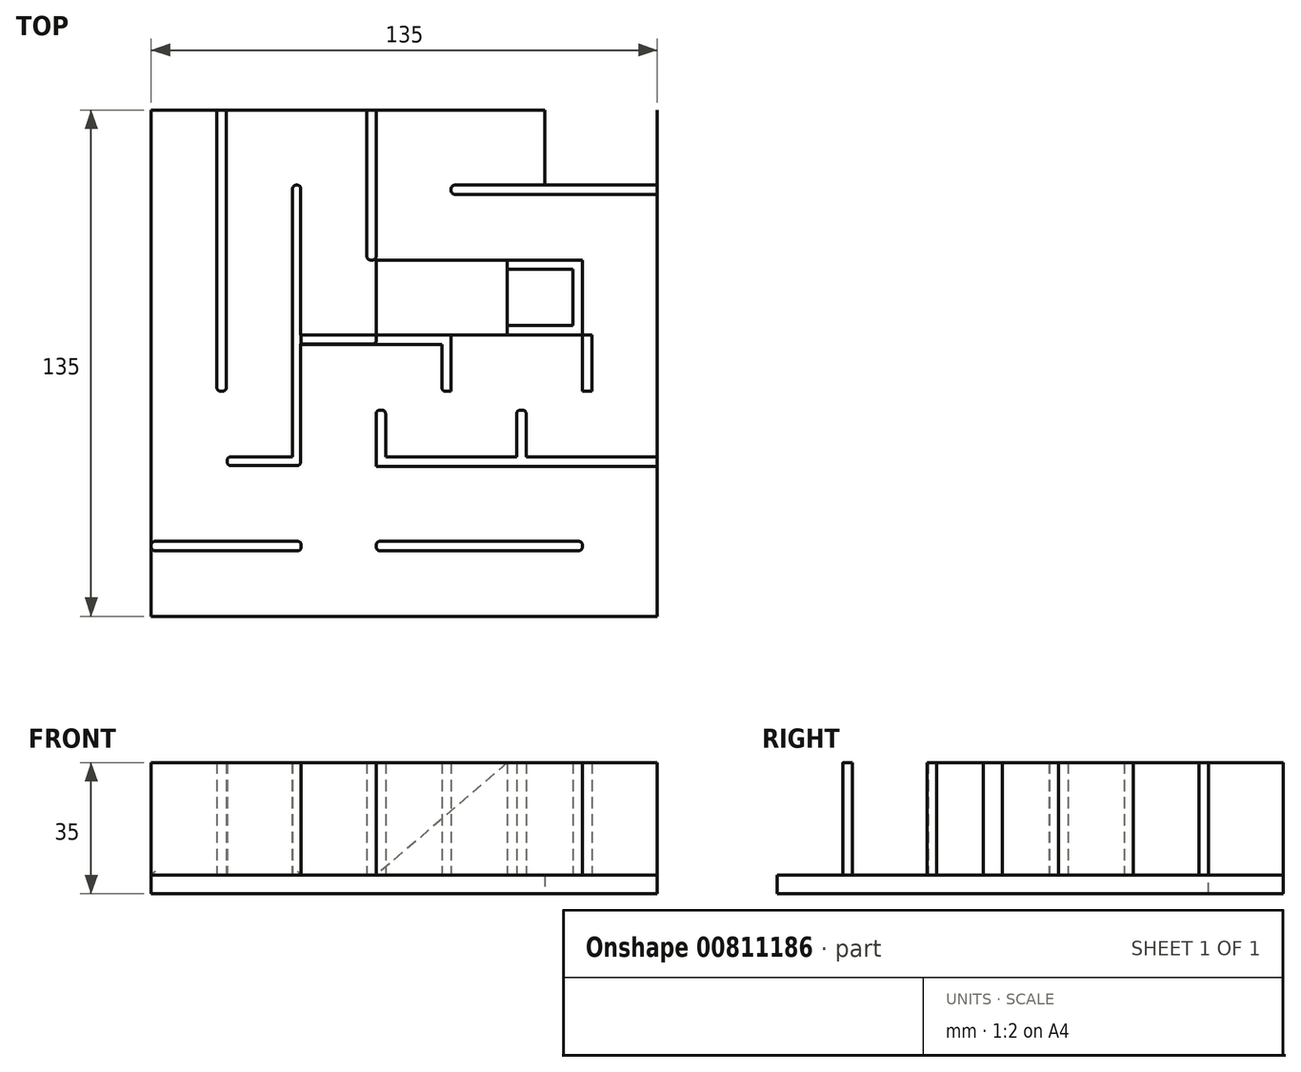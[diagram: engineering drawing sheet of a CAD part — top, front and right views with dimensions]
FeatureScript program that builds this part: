
annotation { "Feature Type Name" : "Feature", "Feature Type Description" : "" }
export const myFeature = defineFeature(function(context is Context, id is Id, definition is map)
    precondition{}
    {
        {
            var Q0;
            Q0=qCreatedBy(makeId("Top.planeOp"),FACE);
            var sketch = newSketch(context, id + "F0", { "sketchPlane" : qUnion([Q0])});
            skLineSegment(sketch, "E0.bottom", {"start": v(-67.5, 67.5) * mm, "end": v(67.5, 67.5) * mm});
            skLineSegment(sketch, "E0.top", {"start": v(-67.5, -67.5) * mm, "end": v(67.5, -67.5) * mm});
            skLineSegment(sketch, "E0.left", {"start": v(-67.5, 67.5) * mm, "end": v(-67.5, -67.5) * mm});
            skLineSegment(sketch, "E0.right", {"start": v(67.5, 67.5) * mm, "end": v(67.5, -67.5) * mm});
            skPoint(sketch, "E0.middle", {"position": v(0, 0) * mm});
            skSolve(sketch);
        }
        {
            var Q0;
            {var subQ2=sQuery(id+"F0.wireOp",EDGE,"E0.top");Q0=makeQuery(id+"F0.imprint","IMPRINT",FACE,{"disambiguationData":[TD([[makeQuery(id+"F0.imprint","IMPRINT",EDGE,{"derivedFrom":subQ2}),1.0]])]});}
            extrude(context, id + "F1", {"entities" : qUnion([Q0]), "depth" : 5 * mm, "offsetDistance" : 25 * mm});
        }
        {
            var Q0;
            Q0=makeQuery(id+"F1.opExtrude","CAP_FACE",FACE,{"disambiguationData":[OSD([sQuery(id+"F0.wireOp",EDGE,"E0.bottom"),sQuery(id+"F0.wireOp",EDGE,"E0.top"),sQuery(id+"F0.wireOp",EDGE,"E0.left"),sQuery(id+"F0.wireOp",EDGE,"E0.right"),sQuery(id+"F0.wireOp",EDGE,"C7zKFyMu-DAGJ-jgr1-EAXP-FvyqHJ8hfMsY"),sQuery(id+"F0.wireOp",EDGE,"vBC2NWEj-7rqq-zskN-MrQE-4xOVSqg6ddvG")])],"isStart":false});
            var sketch = newSketch(context, id + "F2", { "sketchPlane" : qUnion([Q0])});
            skSolve(sketch);
        }
        {
            var Q0;
            Q0=makeQuery(id+"F2.imprint","IMPRINT",FACE,{"disambiguationData":[TD([[makeQuery(id+"F2.imprint","IMPRINT",EDGE,{"derivedFrom":makeQuery(id+"F1.opExtrude","CAP_EDGE",EDGE,{"disambiguationData":[OSD([sQuery(id+"F0.wireOp",EDGE,"E0.bottom")])],"isStart":false})}),-1.0]])]});
            var sketch = newSketch(context, id + "F3", { "sketchPlane" : qUnion([Q0])});
            skLineSegment(sketch, "E1.bottom", {"start": v(-7.5, 27.5) * mm, "end": v(27.5, 27.5) * mm});
            skLineSegment(sketch, "E1.top", {"start": v(-7.5, 7.5) * mm, "end": v(27.5, 7.5) * mm});
            skLineSegment(sketch, "E1.left", {"start": v(-7.5, 27.5) * mm, "end": v(-7.5, 7.5) * mm});
            skLineSegment(sketch, "E1.right", {"start": v(27.5, 27.5) * mm, "end": v(27.5, 7.5) * mm});
            skLineSegment(sketch, "E2", {"start": v(-7.5, 7.5) * mm, "end": v(-27.5, 7.5) * mm});
            skLineSegment(sketch, "E3", {"start": v(-27.5, 7.5) * mm, "end": v(-27.5, 47.5) * mm});
            skLineSegment(sketch, "E4.bottom", {"start": v(-67.5, 67.5) * mm, "end": v(67.5, 67.5) * mm});
            skLineSegment(sketch, "E4.top", {"start": v(-67.5, -67.5) * mm, "end": v(67.5, -67.5) * mm});
            skLineSegment(sketch, "E4.left", {"start": v(-67.5, 67.5) * mm, "end": v(-67.5, -67.5) * mm});
            skLineSegment(sketch, "E4.right", {"start": v(67.5, 67.5) * mm, "end": v(67.5, -67.5) * mm});
            skPoint(sketch, "E4.middle", {"position": v(0, 0) * mm});
            skLineSegment(sketch, "E5", {"start": v(-47.5, 67.5) * mm, "end": v(-47.5, -7.5) * mm});
            skLineSegment(sketch, "E6.bottom", {"start": v(67.5, 67.5) * mm, "end": v(37.5, 67.5) * mm});
            skLineSegment(sketch, "E6.top", {"start": v(67.5, 47.5) * mm, "end": v(37.5, 47.5) * mm});
            skLineSegment(sketch, "E6.left", {"start": v(67.5, 67.5) * mm, "end": v(67.5, 47.5) * mm});
            skLineSegment(sketch, "E6.right", {"start": v(37.5, 67.5) * mm, "end": v(37.5, 47.5) * mm});
            skLineSegment(sketch, "E7", {"start": v(-27.5, 7.5) * mm, "end": v(-27.5, -27.5) * mm});
            skLineSegment(sketch, "E8", {"start": v(-27.5, -27.5) * mm, "end": v(-47.5, -27.5) * mm});
            skLineSegment(sketch, "E9", {"start": v(-67.5, -47.5) * mm, "end": v(-27.5, -47.5) * mm});
            skLineSegment(sketch, "E10", {"start": v(-7.5, -47.5) * mm, "end": v(47.5, -47.5) * mm});
            skLineSegment(sketch, "E11", {"start": v(67.5, -27.5) * mm, "end": v(-7.5, -27.5) * mm});
            skLineSegment(sketch, "E12", {"start": v(-7.5, -27.5) * mm, "end": v(-7.5, -12.5) * mm});
            skLineSegment(sketch, "E13", {"start": v(12.5, 7.63) * mm, "end": v(12.5, -7.5) * mm});
            skLineSegment(sketch, "E14", {"start": v(32.5, -27.5) * mm, "end": v(32.5, -12.5) * mm});
            skLineSegment(sketch, "E15", {"start": v(37.5, 47.5) * mm, "end": v(12.5, 47.5) * mm});
            skLineSegment(sketch, "E16", {"start": v(-7.5, 27.5) * mm, "end": v(-7.5, 67.5) * mm});
            skLineSegment(sketch, "E17.0", {"start": v(-5, -25) * mm, "end": v(-5, -12.5) * mm});
            skLineSegment(sketch, "E17.1", {"start": v(67.5, -25) * mm, "end": v(-5, -25) * mm});
            skLineSegment(sketch, "E18.0", {"start": v(-30, -25) * mm, "end": v(-47.5, -25) * mm});
            skLineSegment(sketch, "E18.1", {"start": v(-30, 7.5) * mm, "end": v(-30, -25) * mm});
            skLineSegment(sketch, "E18.2", {"start": v(-30, 7.5) * mm, "end": v(-30, 47.5) * mm});
            skLineSegment(sketch, "E19.0", {"start": v(-50, 67.5) * mm, "end": v(-50, -7.5) * mm});
            skLineSegment(sketch, "E20.0", {"start": v(-10, 27.5) * mm, "end": v(-10, 67.5) * mm});
            skLineSegment(sketch, "E21.0", {"start": v(-7.5, -50) * mm, "end": v(47.5, -50) * mm});
            skLineSegment(sketch, "E22.0", {"start": v(-67.5, -50) * mm, "end": v(-27.5, -50) * mm});
            skLineSegment(sketch, "E23.0", {"start": v(25.06, 45) * mm, "end": v(12.5, 45) * mm});
            skLineSegment(sketch, "E23.1", {"start": v(67.5, 45) * mm, "end": v(25.06, 45) * mm});
            skLineSegment(sketch, "E24.0", {"start": v(10, 7.63) * mm, "end": v(10, -7.5) * mm});
            skLineSegment(sketch, "E25.0", {"start": v(30, -27.5) * mm, "end": v(30, -12.5) * mm});
            skLineSegment(sketch, "E26.0", {"start": v(-7.5, 5) * mm, "end": v(-27.5, 5) * mm});
            skLineSegment(sketch, "E27", {"start": v(-47.5, -7.5) * mm, "end": v(-50, -7.5) * mm});
            skLineSegment(sketch, "E28", {"start": v(-5, -12.5) * mm, "end": v(-7.5, -12.5) * mm});
            skLineSegment(sketch, "E29", {"start": v(12.5, -7.5) * mm, "end": v(10, -7.5) * mm});
            skLineSegment(sketch, "E30", {"start": v(30, -12.5) * mm, "end": v(32.5, -12.5) * mm});
            skLineSegment(sketch, "E31", {"start": v(-47.5, -27.5) * mm, "end": v(-47.5, -25) * mm});
            skLineSegment(sketch, "E32", {"start": v(-10, 27.5) * mm, "end": v(-7.5, 27.5) * mm});
            skLineSegment(sketch, "E33", {"start": v(-27.5, 47.5) * mm, "end": v(-30, 47.5) * mm});
            skLineSegment(sketch, "E34", {"start": v(12.5, 45) * mm, "end": v(12.5, 47.5) * mm});
            skLineSegment(sketch, "E35", {"start": v(47.5, -50) * mm, "end": v(47.5, -47.5) * mm});
            skLineSegment(sketch, "E36", {"start": v(-7.5, -47.5) * mm, "end": v(-7.5, -50) * mm});
            skLineSegment(sketch, "E37", {"start": v(-27.5, -47.5) * mm, "end": v(-27.5, -50) * mm});
            skLineSegment(sketch, "E38", {"start": v(-27.5, -50) * mm, "end": v(-27.5, -47.5) * mm});
            skLineSegment(sketch, "E39", {"start": v(27.5, 7.5) * mm, "end": v(47.5, 7.5) * mm});
            skLineSegment(sketch, "E40", {"start": v(47.5, 7.5) * mm, "end": v(47.5, 27.5) * mm});
            skLineSegment(sketch, "E41", {"start": v(47.5, 27.5) * mm, "end": v(27.5, 27.5) * mm});
            skPoint(sketch, "E42.end.orphan", {"position": v(67.5, 27.5) * mm});
            skPoint(sketch, "E43.end.orphan", {"position": v(52.5, 27.5) * mm});
            skPoint(sketch, "E44.end.orphan", {"position": v(67.5, 25) * mm});
            skPoint(sketch, "E45.end.orphan", {"position": v(52.5, -7.5) * mm});
            skPoint(sketch, "E46.end.orphan", {"position": v(67.5, -7.5) * mm});
            skLineSegment(sketch, "E47.bottom", {"start": v(50, 7.5) * mm, "end": v(47.5, 7.5) * mm});
            skLineSegment(sketch, "E47.top", {"start": v(50, -7.5) * mm, "end": v(47.5, -7.5) * mm});
            skLineSegment(sketch, "E47.left", {"start": v(47.5, 7.5) * mm, "end": v(47.5, -7.5) * mm});
            skLineSegment(sketch, "E47.right", {"start": v(50, 7.5) * mm, "end": v(50, -7.5) * mm});
            skLineSegment(sketch, "E48", {"start": v(-7.5, 5) * mm, "end": v(10, 5) * mm});
            skLineSegment(sketch, "E49.bottom", {"start": v(27.5, 25) * mm, "end": v(45, 25) * mm});
            skLineSegment(sketch, "E49.top", {"start": v(27.5, 10) * mm, "end": v(45, 10) * mm});
            skLineSegment(sketch, "E49.left", {"start": v(27.5, 25) * mm, "end": v(27.5, 10) * mm});
            skLineSegment(sketch, "E49.right", {"start": v(45, 25) * mm, "end": v(45, 10) * mm});
            skSolve(sketch);
        }
        {
            var Q0;
            Q0=makeQuery(id+"F3.imprint","IMPRINT",FACE,{"disambiguationData":[TD([[makeQuery(id+"F3.imprint","IMPRINT",EDGE,{"derivedFrom":sQuery(id+"F3.wireOp",EDGE,"E1.bottom")}),-1.0]])]});
            extrude(context, id + "F4", {"entities" : qUnion([Q0]), "operationType" : NewBodyOperationType.ADD, "depth" : 30 * mm, "offsetDistance" : 25 * mm});
        }
        {
            var Q0;
            Q0=makeQuery(id+"F4.opExtrude","SWEPT_FACE",FACE,{"disambiguationData":[OSD([sQuery(id+"F3.wireOp",EDGE,"E1.top")])]});
            var sketch = newSketch(context, id + "F5", { "sketchPlane" : qUnion([Q0])});
            skLineSegment(sketch, "E50", {"start": v(27.5, 35) * mm, "end": v(-7.5, 5) * mm});
            skSolve(sketch);
        }
        {
            var Q0;
            Q0=makeQuery(id+"F5.imprint","IMPRINT",FACE,{"disambiguationData":[TD([[makeQuery(id+"F5.imprint","IMPRINT",EDGE,{"derivedFrom":sQuery(id+"F5.wireOp",EDGE,"E50")}),-1.0]])]});
            extrude(context, id + "F6", {"entities" : qUnion([Q0]), "operationType" : NewBodyOperationType.REMOVE, "oppositeDirection" : true, "depth" : 20 * mm, "offsetDistance" : 25 * mm});
        }
        {
            var Q0;
            Q0=makeQuery(id+"F3.imprint","IMPRINT",FACE,{"disambiguationData":[TD([[makeQuery(id+"F3.imprint","IMPRINT",EDGE,{"derivedFrom":sQuery(id+"F3.wireOp",EDGE,"E1.bottom")}),1.0]])]});
            var sketch = newSketch(context, id + "F7", { "sketchPlane" : qUnion([Q0])});
            skLineSegment(sketch, "E51", {"start": v(-7.48, 7.56) * mm, "end": v(-7.48, 5.1) * mm});
            skLineSegment(sketch, "E52", {"start": v(-7.48, 5.1) * mm, "end": v(-27.63, 5.1) * mm});
            skLineSegment(sketch, "E53", {"start": v(-27.63, 5.1) * mm, "end": v(-27.63, 7.49) * mm});
            skLineSegment(sketch, "E54", {"start": v(-27.63, 7.49) * mm, "end": v(-7.48, 7.56) * mm});
            skLineSegment(sketch, "E55", {"start": v(-27.63, 5.1) * mm, "end": v(-27.63, -27.3) * mm});
            skLineSegment(sketch, "E56", {"start": v(-27.63, -27.3) * mm, "end": v(-47.27, -27.3) * mm});
            skLineSegment(sketch, "E57", {"start": v(-47.27, -27.3) * mm, "end": v(-47.27, -24.93) * mm});
            skLineSegment(sketch, "E58", {"start": v(-47.27, -24.93) * mm, "end": v(-29.8, -24.93) * mm});
            skLineSegment(sketch, "E59", {"start": v(-29.8, -24.93) * mm, "end": v(-29.8, 47.57) * mm});
            skLineSegment(sketch, "E60", {"start": v(-29.8, 47.57) * mm, "end": v(-27.63, 47.57) * mm});
            skLineSegment(sketch, "E61", {"start": v(-27.63, 47.57) * mm, "end": v(-27.63, 7.49) * mm});
            skSolve(sketch);
        }
        {
            var Q0;
            Q0=makeQuery(id+"F2.imprint","IMPRINT",FACE,{"disambiguationData":[TD([[makeQuery(id+"F2.imprint","IMPRINT",EDGE,{"derivedFrom":makeQuery(id+"F1.opExtrude","CAP_EDGE",EDGE,{"disambiguationData":[OSD([sQuery(id+"F0.wireOp",EDGE,"E0.bottom")])],"isStart":false})}),-1.0]])]});
            var sketch = newSketch(context, id + "F8", { "sketchPlane" : qUnion([Q0])});
            skLineSegment(sketch, "E62", {"start": v(37.54, 47.53) * mm, "end": v(37.54, 67.57) * mm});
            skLineSegment(sketch, "E63", {"start": v(37.54, 67.57) * mm, "end": v(67.41, 67.57) * mm});
            skLineSegment(sketch, "E64", {"start": v(67.41, 67.57) * mm, "end": v(67.41, 47.53) * mm});
            skLineSegment(sketch, "E65", {"start": v(67.41, 47.53) * mm, "end": v(37.54, 47.53) * mm});
            skSolve(sketch);
        }
        {
            var Q0;
            Q0 = qSketchRegion(id + "F8", true);
            extrude(context, id + "F9", {"entities" : qUnion([Q0]), "operationType" : NewBodyOperationType.REMOVE, "oppositeDirection" : true, "depth" : 50 * mm, "offsetDistance" : 25 * mm});
        }
        {
            var Q0;
            {var subQ0=sQuery(id+"F3.wireOp",EDGE,"E9");Q0=makeQuery(id+"F3.imprint","IMPRINT",FACE,{"disambiguationData":[TD([[makeQuery(id+"F3.imprint","IMPRINT",EDGE,{"derivedFrom":subQ0}),-1.0]])]});}
            var Q1;
            Q1=makeQuery(id+"F3.imprint","IMPRINT",FACE,{"disambiguationData":[TD([[makeQuery(id+"F3.imprint","IMPRINT",EDGE,{"derivedFrom":sQuery(id+"F3.wireOp",EDGE,"E10")}),-1.0]])]});
            var Q2;
            {var subQ0=sQuery(id+"F3.wireOp",EDGE,"E11");var subQ1=sQuery(id+"F3.wireOp",EDGE,"E4.right");var subQ2=makeQuery(id+"F3.imprint","INTERSECT",VERTEX,{"derivedFrom":[subQ1,subQ0]});Q2=makeQuery(id+"F3.imprint","IMPRINT",FACE,{"disambiguationData":[TD([[makeQuery(id+"F3.imprint","IMPRINT",EDGE,{"disambiguationData":[TD([[subQ2,1.0]])],"derivedFrom":subQ1}),-1.0]])]});}
            var Q3;
            {var subQ0=sQuery(id+"F3.wireOp",EDGE,"E30");Q3=makeQuery(id+"F3.imprint","IMPRINT",FACE,{"disambiguationData":[TD([[makeQuery(id+"F3.imprint","IMPRINT",EDGE,{"derivedFrom":subQ0}),-1.0]])]});}
            var Q4;
            {var subQ4=sQuery(id+"F3.wireOp",EDGE,"E12");Q4=makeQuery(id+"F3.imprint","IMPRINT",FACE,{"disambiguationData":[TD([[makeQuery(id+"F3.imprint","IMPRINT",EDGE,{"derivedFrom":subQ4}),-1.0]])]});}
            var Q5;
            {var subQ0=sQuery(id+"F3.wireOp",EDGE,"E14");var subQ1=sQuery(id+"F3.wireOp",EDGE,"E11");var subQ2=makeQuery(id+"F3.imprint","INTERSECT",VERTEX,{"derivedFrom":[subQ1,subQ0]});Q5=makeQuery(id+"F3.imprint","IMPRINT",FACE,{"disambiguationData":[TD([[makeQuery(id+"F3.imprint","IMPRINT",EDGE,{"disambiguationData":[TD([[subQ2,-1.0]])],"derivedFrom":subQ1}),-1.0]])]});}
            var Q6;
            {var subQ9=sQuery(id+"F7.wireOp",EDGE,"E53");Q6=makeQuery(id+"F7.imprint","IMPRINT",FACE,{"disambiguationData":[TD([[makeQuery(id+"F7.imprint","IMPRINT",EDGE,{"derivedFrom":subQ9}),1.0]])]});}
            var Q7;
            {var subQ0=sQuery(id+"F3.wireOp",EDGE,"E5");Q7=makeQuery(id+"F3.imprint","IMPRINT",FACE,{"disambiguationData":[TD([[makeQuery(id+"F3.imprint","IMPRINT",EDGE,{"derivedFrom":subQ0}),-1.0]])]});}
            var Q8;
            {var subQ0=sQuery(id+"F3.wireOp",EDGE,"E6.top");Q8=makeQuery(id+"F3.imprint","IMPRINT",FACE,{"disambiguationData":[TD([[makeQuery(id+"F3.imprint","IMPRINT",EDGE,{"derivedFrom":subQ0}),1.0]])]});}
            var Q9;
            {var subQ1=sQuery(id+"F7.wireOp",EDGE,"E53");Q9=makeQuery(id+"F7.imprint","IMPRINT",FACE,{"disambiguationData":[TD([[makeQuery(id+"F7.imprint","IMPRINT",EDGE,{"derivedFrom":subQ1}),-1.0]])]});}
            var Q10;
            {var subQ0=sQuery(id+"F3.wireOp",EDGE,"E16");Q10=makeQuery(id+"F3.imprint","IMPRINT",FACE,{"disambiguationData":[TD([[makeQuery(id+"F3.imprint","IMPRINT",EDGE,{"derivedFrom":subQ0}),1.0]])]});}
            var Q11;
            {var subQ5=sQuery(id+"F3.wireOp",EDGE,"E29");Q11=makeQuery(id+"F3.imprint","IMPRINT",FACE,{"disambiguationData":[TD([[makeQuery(id+"F3.imprint","IMPRINT",EDGE,{"derivedFrom":subQ5}),-1.0]])]});}
            var Q12;
            Q12=makeQuery(id+"F3.imprint","IMPRINT",FACE,{"disambiguationData":[TD([[makeQuery(id+"F3.imprint","IMPRINT",EDGE,{"derivedFrom":sQuery(id+"F3.wireOp",EDGE,"E47.bottom")}),1.0]])]});
            var Q13;
            {var subQ5=sQuery(id+"F3.wireOp",EDGE,"E2");Q13=makeQuery(id+"F3.imprint","IMPRINT",FACE,{"disambiguationData":[TD([[makeQuery(id+"F3.imprint","IMPRINT",EDGE,{"derivedFrom":subQ5}),1.0]])]});}
            var Q14;
            {var subQ4=sQuery(id+"F3.wireOp",EDGE,"E39");Q14=makeQuery(id+"F3.imprint","IMPRINT",FACE,{"disambiguationData":[TD([[makeQuery(id+"F3.imprint","IMPRINT",EDGE,{"derivedFrom":subQ4}),1.0]])]});}
            extrude(context, id + "F10", {"entities" : qUnion([Q0, Q1, Q2, Q3, Q4, Q5, Q6, Q7, Q8, Q9, Q10, Q11, Q12, Q13, Q14]), "depth" : 30 * mm, "offsetDistance" : 25 * mm});
        }
        {
            var Q0;
            Q0=makeQuery(id+"F10.opExtrude","SWEPT_EDGE",EDGE,{"disambiguationData":[OSD([sQuery(id+"F3.wireOp",EDGE,"E15"),sQuery(id+"F3.wireOp",EDGE,"E34")])]});
            var Q1;
            Q1=makeQuery(id+"F10.opExtrude","SWEPT_EDGE",EDGE,{"disambiguationData":[OSD([sQuery(id+"F3.wireOp",EDGE,"E23.0"),sQuery(id+"F3.wireOp",EDGE,"E34")])]});
            var Q2;
            Q2=makeQuery(id+"F10.opExtrude","SWEPT_EDGE",EDGE,{"disambiguationData":[OSD([sQuery(id+"F3.wireOp",EDGE,"E20.0"),sQuery(id+"F3.wireOp",EDGE,"E32")])]});
            var Q3;
            Q3=makeQuery(id+"F10.opExtrude","SWEPT_EDGE",EDGE,{"disambiguationData":[OSD([sQuery(id+"F3.wireOp",EDGE,"E33"),sQuery(id+"F7.wireOp",EDGE,"E59")])]});
            var Q4;
            Q4=makeQuery(id+"F10.opExtrude","SWEPT_EDGE",EDGE,{"disambiguationData":[OSD([sQuery(id+"F3.wireOp",EDGE,"E33"),sQuery(id+"F7.wireOp",EDGE,"E61")])]});
            var Q5;
            Q5=makeQuery(id+"F10.opExtrude","SWEPT_EDGE",EDGE,{"disambiguationData":[OSD([sQuery(id+"F3.wireOp",EDGE,"E1.top"),sQuery(id+"F3.wireOp",EDGE,"E1.left"),sQuery(id+"F3.wireOp",EDGE,"E2"),sQuery(id+"F3.wireOp",EDGE,"XGEKfM7I-rLZ4-EBif-T8fQ-5XQJKHtAgi8g")])]});
            var Q6;
            Q6=makeQuery(id+"F10.opExtrude","SWEPT_EDGE",EDGE,{"disambiguationData":[OSD([sQuery(id+"F3.wireOp",EDGE,"E19.0"),sQuery(id+"F3.wireOp",EDGE,"E27")])]});
            var Q7;
            Q7=makeQuery(id+"F10.opExtrude","SWEPT_EDGE",EDGE,{"disambiguationData":[OSD([sQuery(id+"F3.wireOp",EDGE,"E18.0"),sQuery(id+"F7.wireOp",EDGE,"E57")])]});
            var Q8;
            Q8=makeQuery(id+"F10.opExtrude","CAP_EDGE",EDGE,{"disambiguationData":[OSD([sQuery(id+"F3.wireOp",EDGE,"E9")])],"isStart":true});
            var Q9;
            Q9=makeQuery(id+"F10.opExtrude","SWEPT_EDGE",EDGE,{"disambiguationData":[OSD([sQuery(id+"F3.wireOp",EDGE,"E12"),sQuery(id+"F3.wireOp",EDGE,"E28")])]});
            var Q10;
            Q10=makeQuery(id+"F10.opExtrude","SWEPT_EDGE",EDGE,{"disambiguationData":[OSD([sQuery(id+"F3.wireOp",EDGE,"E17.0"),sQuery(id+"F3.wireOp",EDGE,"E28")])]});
            var Q11;
            Q11=makeQuery(id+"F10.opExtrude","SWEPT_EDGE",EDGE,{"disambiguationData":[OSD([sQuery(id+"F3.wireOp",EDGE,"E25.0"),sQuery(id+"F3.wireOp",EDGE,"E30")])]});
            var Q12;
            Q12=makeQuery(id+"F10.opExtrude","SWEPT_EDGE",EDGE,{"disambiguationData":[OSD([sQuery(id+"F3.wireOp",EDGE,"E14"),sQuery(id+"F3.wireOp",EDGE,"E30")])]});
            var Q13;
            Q13=makeQuery(id+"F10.opExtrude","SWEPT_EDGE",EDGE,{"disambiguationData":[OSD([sQuery(id+"F3.wireOp",EDGE,"E9"),sQuery(id+"F3.wireOp",EDGE,"E38")])]});
            var Q14;
            Q14=makeQuery(id+"F10.opExtrude","SWEPT_EDGE",EDGE,{"disambiguationData":[OSD([sQuery(id+"F3.wireOp",EDGE,"E10"),sQuery(id+"F3.wireOp",EDGE,"E36")])]});
            var Q15;
            Q15=makeQuery(id+"F10.opExtrude","SWEPT_EDGE",EDGE,{"disambiguationData":[OSD([sQuery(id+"F3.wireOp",EDGE,"E21.0"),sQuery(id+"F3.wireOp",EDGE,"E36")])]});
            var Q16;
            Q16=makeQuery(id+"F10.opExtrude","SWEPT_EDGE",EDGE,{"disambiguationData":[OSD([sQuery(id+"F3.wireOp",EDGE,"E24.0"),sQuery(id+"F3.wireOp",EDGE,"E29")])]});
            var Q17;
            Q17=makeQuery(id+"F10.opExtrude","SWEPT_EDGE",EDGE,{"disambiguationData":[OSD([sQuery(id+"F3.wireOp",EDGE,"XGEKfM7I-rLZ4-EBif-T8fQ-5XQJKHtAgi8g"),sQuery(id+"F7.wireOp",EDGE,"E52")])]});
            var Q18;
            Q18=makeQuery(id+"F10.opExtrude","SWEPT_EDGE",EDGE,{"disambiguationData":[OSD([sQuery(id+"F7.wireOp",EDGE,"E55"),sQuery(id+"F7.wireOp",EDGE,"E56")])]});
            var Q19;
            Q19=makeQuery(id+"F10.opExtrude","SWEPT_EDGE",EDGE,{"disambiguationData":[OSD([sQuery(id+"F3.wireOp",EDGE,"E22.0"),sQuery(id+"F3.wireOp",EDGE,"E38")])]});
            var Q20;
            Q20=makeQuery(id+"F10.opExtrude","SWEPT_EDGE",EDGE,{"disambiguationData":[OSD([sQuery(id+"F3.wireOp",EDGE,"E5"),sQuery(id+"F3.wireOp",EDGE,"E27")])]});
            var Q21;
            Q21=makeQuery(id+"F10.opExtrude","SWEPT_EDGE",EDGE,{"disambiguationData":[OSD([sQuery(id+"F7.wireOp",EDGE,"E56"),sQuery(id+"F7.wireOp",EDGE,"E57")])]});
            var Q22;
            Q22=makeQuery(id+"F10.opExtrude","SWEPT_EDGE",EDGE,{"disambiguationData":[OSD([sQuery(id+"F3.wireOp",EDGE,"E21.0"),sQuery(id+"F3.wireOp",EDGE,"E35")])]});
            var Q23;
            Q23=makeQuery(id+"F10.opExtrude","SWEPT_EDGE",EDGE,{"disambiguationData":[OSD([sQuery(id+"F3.wireOp",EDGE,"E10"),sQuery(id+"F3.wireOp",EDGE,"E35")])]});
            var Q24;
            Q24=makeQuery(id+"F10.opExtrude","SWEPT_EDGE",EDGE,{"disambiguationData":[OSD([sQuery(id+"F3.wireOp",EDGE,"E1.bottom"),sQuery(id+"F3.wireOp",EDGE,"E1.left"),sQuery(id+"F3.wireOp",EDGE,"E16"),sQuery(id+"F3.wireOp",EDGE,"E32")])]});
            fillet(context, id + "F11", {"entities" : qUnion([Q0, Q1, Q2, Q3, Q4, Q5, Q6, Q7, Q8, Q9, Q10, Q11, Q12, Q13, Q14, Q15, Q16, Q17, Q18, Q19, Q20, Q21, Q22, Q23, Q24]), "radius" : 1 * mm, "tangentPropagation" : true, "allowEdgeOverflow" : false});
        }
    });
